# Revit family: WH2898
name_source: partatom
category: Plumbing Fixtures
units: mm (PartAtom-declared; Revit-internal decimal feet)

## family parameters
Cut with Voids When Loaded = No
Host = Face
OmniClass Number = 23.45.05.21.11.11
OmniClass Title = Water Operated Water Closets
Part Type = Normal
Room Calculation Point = No
Round Connector Dimension = Use Diameter
Shared = Yes

## types (5) — shared parameters
ADA Compliant = Yes
Assembly Code = D2010110
CW Connection = Yes
CWFU = 10
Cold Water Connection Diameter = 1"
Cold Water Connection Radius = 1/2"
Default Elevation = 0"
HW Connection = No
Height = 17"
Length = 2"
Manufacturer = Whitehall Mfg
Material = Stainless-Whitehall-16 Gauge-White
Product Documentation Link = https://www.whitehallmfg.com
Product Page URL = https://www.whitehallmfg.com
Revised Date = 08/19/2019
URL = http://www.whitehallmfg.com
Vent Connection = No
WFU = 10
Waste Connection = Yes
Waste Connection Diameter = 2 1/8"
Waste Connection Radius = 1 1/16"
Width = 17"
zero-valued in all types: HWFU

## per-type parameters (varying)
| type | Description | Flush Rate | Flush Valve and Punch |
| WH2898-EG10-1.28 | Ligature Resistant Flush Valve Cover With 1.28 GPF Hydraulic Flush Valve (White) | 1.28 GPF | Yes |
| WH2898-EG10-1.6 | Ligature Resistant Flush Valve Cover With 1.6 GPF Hydraulic Flush Valve (White) | 1.6 GPF | Yes |
| WH2898-EG10-0.5 | Ligature Resistant Flush Valve Cover With 0.5 GPF Hydraulic Flush Valve (White) | 0.5 GPF | Yes |
| WH2898-EG10-0.125 | Ligature Resistant Flush Valve Cover With 0.125 GPF Hydraulic Flush Valve (White) | 0.125 GPF | Yes |
| WH2898-BLANK | Ligature Resistant Flush Valve Cover With 1.6 GPF Hydraulic Flush Valve (White) |  | No |

note: column(s) folded — value = type name in every type: Model

## geometry (parser evidence)
native form markers: Sweep x3
no freeform markers — native parametric forms only
